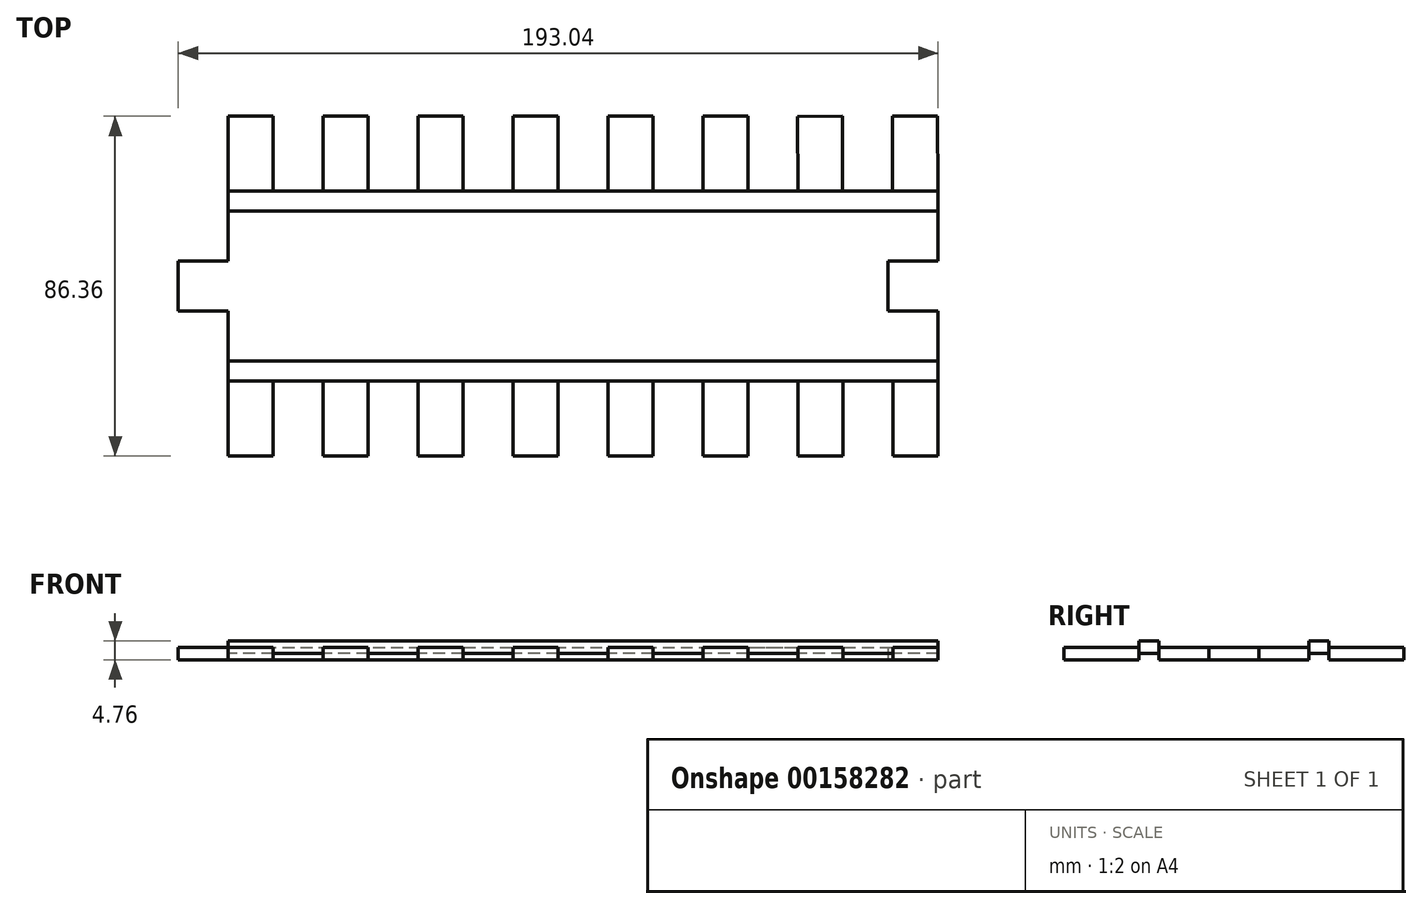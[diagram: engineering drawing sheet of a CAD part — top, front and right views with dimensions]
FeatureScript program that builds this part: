
annotation { "Feature Type Name" : "Feature", "Feature Type Description" : "" }
export const myFeature = defineFeature(function(context is Context, id is Id, definition is map)
    precondition{}
    {
        {
            var Q0;
            Q0=qCreatedBy(makeId("Top.planeOp"),FACE);
            var sketch = newSketch(context, id + "F0", { "sketchPlane" : qUnion([Q0])});
            skLineSegment(sketch, "E0", {"start": v(-90.1, -5.08) * mm, "end": v(-90.1, -24.13) * mm});
            skLineSegment(sketch, "E1", {"start": v(-90.1, -24.13) * mm, "end": v(-78.67, -24.13) * mm});
            skLineSegment(sketch, "E2", {"start": v(-78.67, -24.13) * mm, "end": v(-78.67, -5.08) * mm});
            skLineSegment(sketch, "E3", {"start": v(-65.97, -5.08) * mm, "end": v(-65.97, -24.13) * mm});
            skLineSegment(sketch, "E4", {"start": v(-65.97, -24.13) * mm, "end": v(-54.54, -24.13) * mm});
            skLineSegment(sketch, "E5", {"start": v(-54.54, -24.13) * mm, "end": v(-54.54, -5.08) * mm});
            skLineSegment(sketch, "E6", {"start": v(-41.84, -5.08) * mm, "end": v(-41.84, -24.13) * mm});
            skLineSegment(sketch, "E7", {"start": v(-41.84, -24.13) * mm, "end": v(-30.41, -24.13) * mm});
            skLineSegment(sketch, "E8", {"start": v(-30.41, -24.13) * mm, "end": v(-30.41, -5.08) * mm});
            skLineSegment(sketch, "E9", {"start": v(-17.71, -5.08) * mm, "end": v(-17.71, -24.13) * mm});
            skLineSegment(sketch, "E10", {"start": v(-17.71, -24.13) * mm, "end": v(-6.28, -24.13) * mm});
            skLineSegment(sketch, "E11", {"start": v(-6.28, -24.13) * mm, "end": v(-6.28, -5.08) * mm});
            skLineSegment(sketch, "E12", {"start": v(6.42, -5.08) * mm, "end": v(6.42, -24.13) * mm});
            skLineSegment(sketch, "E13", {"start": v(6.42, -24.13) * mm, "end": v(17.85, -24.13) * mm});
            skLineSegment(sketch, "E14", {"start": v(17.85, -24.13) * mm, "end": v(17.85, -5.08) * mm});
            skLineSegment(sketch, "E15", {"start": v(30.55, -5.08) * mm, "end": v(30.55, -24.13) * mm});
            skLineSegment(sketch, "E16", {"start": v(30.55, -24.13) * mm, "end": v(41.98, -24.13) * mm});
            skLineSegment(sketch, "E17", {"start": v(41.98, -24.13) * mm, "end": v(41.98, -5.08) * mm});
            skLineSegment(sketch, "E18", {"start": v(90.24, -5.08) * mm, "end": v(90.24, -24.13) * mm});
            skLineSegment(sketch, "E19", {"start": v(90.24, -24.13) * mm, "end": v(78.8, -24.13) * mm});
            skLineSegment(sketch, "E20", {"start": v(78.8, -24.13) * mm, "end": v(78.8, -5.08) * mm});
            skLineSegment(sketch, "E21", {"start": v(66.1, -5.08) * mm, "end": v(66.1, -24.13) * mm});
            skLineSegment(sketch, "E22", {"start": v(66.1, -24.13) * mm, "end": v(54.68, -24.13) * mm});
            skLineSegment(sketch, "E23", {"start": v(54.68, -24.13) * mm, "end": v(54.68, -5.08) * mm});
            skLineSegment(sketch, "E24", {"start": v(-90.1, -5.08) * mm, "end": v(-90.1, 0) * mm});
            skLineSegment(sketch, "E25", {"start": v(-90.1, 0) * mm, "end": v(90.24, 0) * mm});
            skLineSegment(sketch, "E26", {"start": v(90.24, 0) * mm, "end": v(90.24, -5.08) * mm});
            skLineSegment(sketch, "E27", {"start": v(90.24, -5.08) * mm, "end": v(-90.1, -5.08) * mm});
            skLineSegment(sketch, "E28", {"start": v(90.24, 0) * mm, "end": v(90.24, 12.7) * mm});
            skLineSegment(sketch, "E29", {"start": v(90.24, 12.7) * mm, "end": v(77.54, 12.7) * mm});
            skLineSegment(sketch, "E30", {"start": v(77.54, 12.7) * mm, "end": v(77.54, 25.4) * mm});
            skLineSegment(sketch, "E31", {"start": v(77.54, 25.4) * mm, "end": v(90.24, 25.4) * mm});
            skLineSegment(sketch, "E32", {"start": v(90.24, 25.4) * mm, "end": v(90.24, 38.1) * mm});
            skLineSegment(sketch, "E33", {"start": v(-90.1, 0) * mm, "end": v(-90.1, 12.7) * mm});
            skLineSegment(sketch, "E34", {"start": v(-90.1, 12.7) * mm, "end": v(-102.8, 12.7) * mm});
            skLineSegment(sketch, "E35", {"start": v(-102.8, 12.7) * mm, "end": v(-102.8, 25.4) * mm});
            skLineSegment(sketch, "E36", {"start": v(-102.8, 25.4) * mm, "end": v(-90.1, 25.4) * mm});
            skLineSegment(sketch, "E37", {"start": v(-90.1, 25.4) * mm, "end": v(-90.1, 38.1) * mm});
            skLineSegment(sketch, "E38", {"start": v(-90.1, 38.1) * mm, "end": v(90.24, 38.1) * mm});
            skLineSegment(sketch, "E39", {"start": v(-90.1, 38.1) * mm, "end": v(-90.1, 43.18) * mm});
            skLineSegment(sketch, "E40", {"start": v(-90.1, 43.18) * mm, "end": v(90.24, 43.18) * mm});
            skLineSegment(sketch, "E41", {"start": v(90.24, 43.18) * mm, "end": v(90.24, 38.1) * mm});
            skLineSegment(sketch, "E42.MirrorCS", {"start": v(-78.65, -24.13) * mm, "end": v(-78.65, -5.08) * mm});
            skLineSegment(sketch, "E43", {"start": v(-90.1, 43.18) * mm, "end": v(-90.1, 62.23) * mm});
            skLineSegment(sketch, "E44", {"start": v(-90.1, 62.23) * mm, "end": v(-78.67, 62.23) * mm});
            skLineSegment(sketch, "E45", {"start": v(-78.67, 62.23) * mm, "end": v(-78.67, 43.18) * mm});
            skLineSegment(sketch, "E46", {"start": v(-78.67, -5.08) * mm, "end": v(-65.97, -5.08) * mm});
            skLineSegment(sketch, "E47", {"start": v(-54.54, -5.08) * mm, "end": v(-41.84, -5.08) * mm});
            skLineSegment(sketch, "E48", {"start": v(-30.41, -5.08) * mm, "end": v(-17.71, -5.08) * mm});
            skLineSegment(sketch, "E49", {"start": v(-6.28, -5.08) * mm, "end": v(6.42, -5.08) * mm});
            skLineSegment(sketch, "E50", {"start": v(17.85, -5.08) * mm, "end": v(30.55, -5.08) * mm});
            skLineSegment(sketch, "E51", {"start": v(41.98, -5.08) * mm, "end": v(54.68, -5.08) * mm});
            skLineSegment(sketch, "E52", {"start": v(66.1, -5.08) * mm, "end": v(78.8, -5.08) * mm});
            skLineSegment(sketch, "E53", {"start": v(-78.67, 43.18) * mm, "end": v(-65.97, 43.18) * mm});
            skLineSegment(sketch, "E54", {"start": v(-65.97, 43.18) * mm, "end": v(-65.97, 62.23) * mm});
            skLineSegment(sketch, "E55", {"start": v(-65.97, 62.23) * mm, "end": v(-54.54, 62.23) * mm});
            skLineSegment(sketch, "E56", {"start": v(-54.54, 62.23) * mm, "end": v(-54.54, 43.18) * mm});
            skLineSegment(sketch, "E57", {"start": v(-54.54, 43.18) * mm, "end": v(-41.84, 43.18) * mm});
            skLineSegment(sketch, "E58", {"start": v(-41.84, 43.18) * mm, "end": v(-41.84, 62.23) * mm});
            skLineSegment(sketch, "E59", {"start": v(-41.84, 62.23) * mm, "end": v(-30.41, 62.23) * mm});
            skLineSegment(sketch, "E60", {"start": v(-30.41, 62.23) * mm, "end": v(-30.41, 43.18) * mm});
            skLineSegment(sketch, "E61", {"start": v(-30.41, 43.18) * mm, "end": v(-17.71, 43.18) * mm});
            skLineSegment(sketch, "E62", {"start": v(-17.71, 43.18) * mm, "end": v(-17.71, 62.23) * mm});
            skLineSegment(sketch, "E63", {"start": v(-17.71, 62.23) * mm, "end": v(-6.28, 62.23) * mm});
            skLineSegment(sketch, "E64", {"start": v(-6.28, 62.23) * mm, "end": v(-6.28, 43.18) * mm});
            skLineSegment(sketch, "E65", {"start": v(-6.28, 43.18) * mm, "end": v(6.42, 43.18) * mm});
            skLineSegment(sketch, "E66", {"start": v(6.42, 43.18) * mm, "end": v(6.42, 62.23) * mm});
            skLineSegment(sketch, "E67", {"start": v(6.42, 62.23) * mm, "end": v(17.85, 62.23) * mm});
            skLineSegment(sketch, "E68", {"start": v(17.85, 62.23) * mm, "end": v(17.85, 43.18) * mm});
            skLineSegment(sketch, "E69", {"start": v(17.85, 43.18) * mm, "end": v(30.55, 43.18) * mm});
            skLineSegment(sketch, "E70", {"start": v(30.55, 43.18) * mm, "end": v(30.55, 62.23) * mm});
            skLineSegment(sketch, "E71", {"start": v(30.55, 62.23) * mm, "end": v(41.98, 62.23) * mm});
            skLineSegment(sketch, "E72", {"start": v(41.98, 62.23) * mm, "end": v(41.98, 43.18) * mm});
            skLineSegment(sketch, "E73", {"start": v(41.98, 43.18) * mm, "end": v(54.68, 43.28) * mm});
            skLineSegment(sketch, "E74", {"start": v(54.68, 43.28) * mm, "end": v(54.53, 62.14) * mm});
            skLineSegment(sketch, "E75", {"start": v(54.53, 62.14) * mm, "end": v(65.96, 62.23) * mm});
            skLineSegment(sketch, "E76", {"start": v(65.96, 62.23) * mm, "end": v(65.96, 43.18) * mm});
            skLineSegment(sketch, "E77", {"start": v(65.96, 43.18) * mm, "end": v(78.66, 43.18) * mm});
            skLineSegment(sketch, "E78", {"start": v(78.66, 43.18) * mm, "end": v(78.66, 62.23) * mm});
            skLineSegment(sketch, "E79", {"start": v(78.66, 62.23) * mm, "end": v(90.1, 62.23) * mm});
            skLineSegment(sketch, "E80", {"start": v(90.1, 62.23) * mm, "end": v(90.24, 43.18) * mm});
            skSolve(sketch);
        }
        {
            var Q0;
            {var subQ0=sQuery(id+"F0.wireOp",EDGE,"E43");Q0=makeQuery(id+"F0.imprint","IMPRINT",FACE,{"disambiguationData":[TD([[makeQuery(id+"F0.imprint","IMPRINT",EDGE,{"derivedFrom":subQ0}),-1.0]])]});}
            var Q1;
            {var subQ0=sQuery(id+"F0.wireOp",EDGE,"E54");Q1=makeQuery(id+"F0.imprint","IMPRINT",FACE,{"disambiguationData":[TD([[makeQuery(id+"F0.imprint","IMPRINT",EDGE,{"derivedFrom":subQ0}),-1.0]])]});}
            var Q2;
            {var subQ0=sQuery(id+"F0.wireOp",EDGE,"E58");Q2=makeQuery(id+"F0.imprint","IMPRINT",FACE,{"disambiguationData":[TD([[makeQuery(id+"F0.imprint","IMPRINT",EDGE,{"derivedFrom":subQ0}),-1.0]])]});}
            var Q3;
            {var subQ0=sQuery(id+"F0.wireOp",EDGE,"E62");Q3=makeQuery(id+"F0.imprint","IMPRINT",FACE,{"disambiguationData":[TD([[makeQuery(id+"F0.imprint","IMPRINT",EDGE,{"derivedFrom":subQ0}),-1.0]])]});}
            var Q4;
            {var subQ0=sQuery(id+"F0.wireOp",EDGE,"E66");Q4=makeQuery(id+"F0.imprint","IMPRINT",FACE,{"disambiguationData":[TD([[makeQuery(id+"F0.imprint","IMPRINT",EDGE,{"derivedFrom":subQ0}),-1.0]])]});}
            var Q5;
            {var subQ0=sQuery(id+"F0.wireOp",EDGE,"E70");Q5=makeQuery(id+"F0.imprint","IMPRINT",FACE,{"disambiguationData":[TD([[makeQuery(id+"F0.imprint","IMPRINT",EDGE,{"derivedFrom":subQ0}),-1.0]])]});}
            var Q6;
            {var subQ0=sQuery(id+"F0.wireOp",EDGE,"E73");Q6=makeQuery(id+"F0.imprint","IMPRINT",FACE,{"disambiguationData":[TD([[makeQuery(id+"F0.imprint","IMPRINT",EDGE,{"derivedFrom":subQ0}),-1.0]])]});}
            var Q7;
            {var subQ2=sQuery(id+"F0.wireOp",EDGE,"E78");Q7=makeQuery(id+"F0.imprint","IMPRINT",FACE,{"disambiguationData":[TD([[makeQuery(id+"F0.imprint","IMPRINT",EDGE,{"derivedFrom":subQ2}),-1.0]])]});}
            var Q8;
            {var subQ0=sQuery(id+"F0.wireOp",EDGE,"E18");Q8=makeQuery(id+"F0.imprint","IMPRINT",FACE,{"disambiguationData":[TD([[makeQuery(id+"F0.imprint","IMPRINT",EDGE,{"derivedFrom":subQ0}),-1.0]])]});}
            var Q9;
            {var subQ0=sQuery(id+"F0.wireOp",EDGE,"E21");Q9=makeQuery(id+"F0.imprint","IMPRINT",FACE,{"disambiguationData":[TD([[makeQuery(id+"F0.imprint","IMPRINT",EDGE,{"derivedFrom":subQ0}),-1.0]])]});}
            var Q10;
            {var subQ0=sQuery(id+"F0.wireOp",EDGE,"E15");Q10=makeQuery(id+"F0.imprint","IMPRINT",FACE,{"disambiguationData":[TD([[makeQuery(id+"F0.imprint","IMPRINT",EDGE,{"derivedFrom":subQ0}),1.0]])]});}
            var Q11;
            {var subQ0=sQuery(id+"F0.wireOp",EDGE,"E12");Q11=makeQuery(id+"F0.imprint","IMPRINT",FACE,{"disambiguationData":[TD([[makeQuery(id+"F0.imprint","IMPRINT",EDGE,{"derivedFrom":subQ0}),1.0]])]});}
            var Q12;
            {var subQ0=sQuery(id+"F0.wireOp",EDGE,"E9");Q12=makeQuery(id+"F0.imprint","IMPRINT",FACE,{"disambiguationData":[TD([[makeQuery(id+"F0.imprint","IMPRINT",EDGE,{"derivedFrom":subQ0}),1.0]])]});}
            var Q13;
            {var subQ0=sQuery(id+"F0.wireOp",EDGE,"E6");Q13=makeQuery(id+"F0.imprint","IMPRINT",FACE,{"disambiguationData":[TD([[makeQuery(id+"F0.imprint","IMPRINT",EDGE,{"derivedFrom":subQ0}),1.0]])]});}
            var Q14;
            {var subQ0=sQuery(id+"F0.wireOp",EDGE,"E3");Q14=makeQuery(id+"F0.imprint","IMPRINT",FACE,{"disambiguationData":[TD([[makeQuery(id+"F0.imprint","IMPRINT",EDGE,{"derivedFrom":subQ0}),1.0]])]});}
            var Q15;
            {var subQ0=sQuery(id+"F0.wireOp",EDGE,"E0");Q15=makeQuery(id+"F0.imprint","IMPRINT",FACE,{"disambiguationData":[TD([[makeQuery(id+"F0.imprint","IMPRINT",EDGE,{"derivedFrom":subQ0}),1.0]])]});}
            var Q16;
            Q16=makeQuery(id+"F0.imprint","IMPRINT",FACE,{"disambiguationData":[TD([[makeQuery(id+"F0.imprint","IMPRINT",EDGE,{"derivedFrom":sQuery(id+"F0.wireOp",EDGE,"E25")}),1.0]])]});
            extrude(context, id + "F1", {"entities" : qUnion([Q0, Q1, Q2, Q3, Q4, Q5, Q6, Q7, Q8, Q9, Q10, Q11, Q12, Q13, Q14, Q15, Q16]), "endBound" : BoundingType.SYMMETRIC, "depth" : 3.17 * mm});
        }
        {
            var Q0;
            Q0=makeQuery(id+"F0.imprint","IMPRINT",FACE,{"disambiguationData":[TD([[makeQuery(id+"F0.imprint","IMPRINT",EDGE,{"derivedFrom":sQuery(id+"F0.wireOp",EDGE,"E38")}),1.0]])]});
            var Q1;
            {var subQ10=sQuery(id+"F0.wireOp",EDGE,"E24");Q1=makeQuery(id+"F0.imprint","IMPRINT",FACE,{"disambiguationData":[TD([[makeQuery(id+"F0.imprint","IMPRINT",EDGE,{"derivedFrom":subQ10}),-1.0]])]});}
            extrude(context, id + "F2", {"entities" : qUnion([Q0, Q1]), "depth" : 3.17 * mm});
        }
    });
